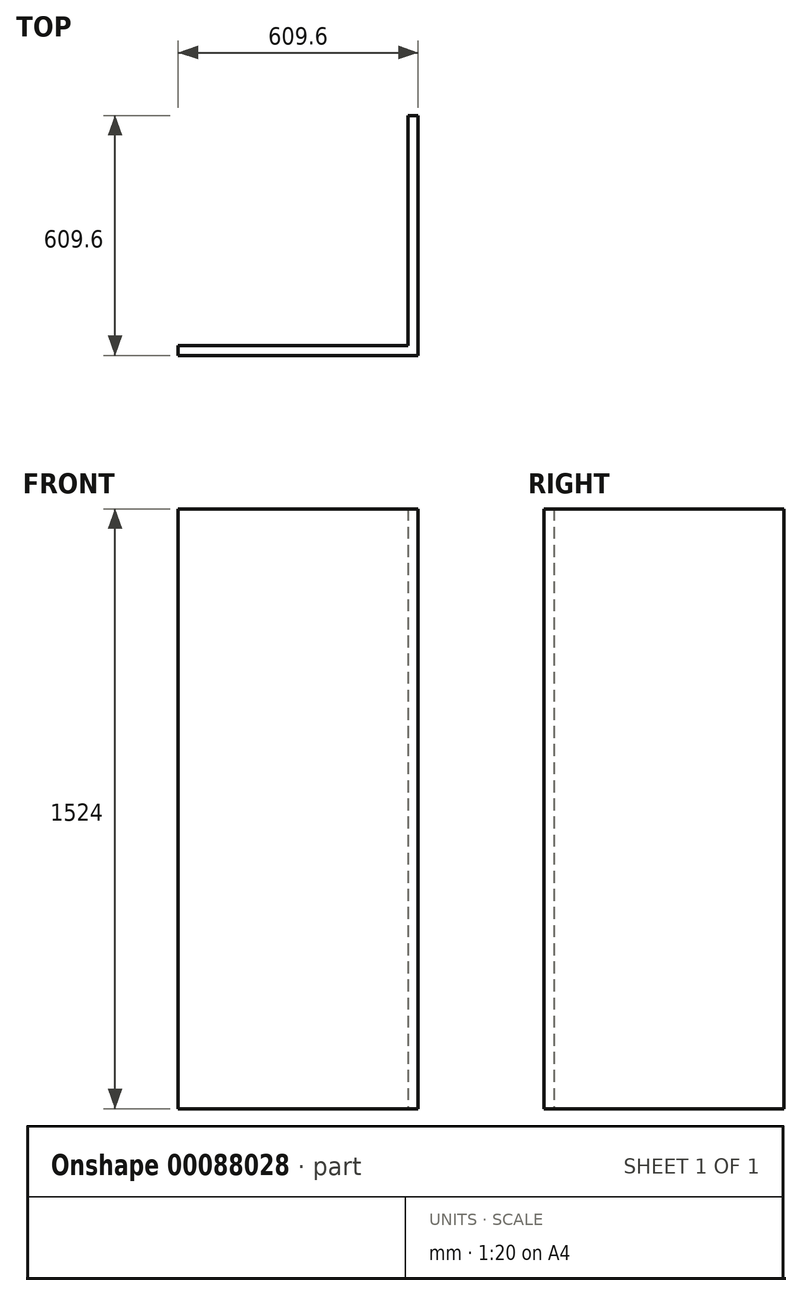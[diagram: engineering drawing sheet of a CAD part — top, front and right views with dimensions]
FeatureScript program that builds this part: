
annotation { "Feature Type Name" : "Feature", "Feature Type Description" : "" }
export const myFeature = defineFeature(function(context is Context, id is Id, definition is map)
    precondition{}
    {
        {
            var Q0;
            Q0=qCreatedBy(makeId("Top.planeOp"),FACE);
            var sketch = newSketch(context, id + "F0", { "sketchPlane" : qUnion([Q0])});
            skLineSegment(sketch, "E0", {"start": v(0, 0) * mm, "end": v(-609.6, 0) * mm});
            skLineSegment(sketch, "E1", {"start": v(0, 609.6) * mm, "end": v(0, 0) * mm});
            skLineSegment(sketch, "E2", {"start": v(-25.4, 609.6) * mm, "end": v(-25.4, 25.4) * mm});
            skLineSegment(sketch, "E3", {"start": v(-25.4, 25.4) * mm, "end": v(-609.6, 25.4) * mm});
            skLineSegment(sketch, "E4", {"start": v(-609.6, 0) * mm, "end": v(-609.6, 25.4) * mm});
            skLineSegment(sketch, "E5", {"start": v(-25.4, 609.6) * mm, "end": v(0, 609.6) * mm});
            skLineSegment(sketch, "E6", {"start": v(-180.41, 25.4) * mm, "end": v(-180.41, 0) * mm, "construction": true});
            skLineSegment(sketch, "E7", {"start": v(-25.4, 131.67) * mm, "end": v(0, 131.67) * mm, "construction": true});
            skSolve(sketch);
        }
        {
            var Q0;
            Q0=makeQuery(id+"F0.imprint","IMPRINT",FACE,{"disambiguationData":[TD([[makeQuery(id+"F0.imprint","IMPRINT",EDGE,{"derivedFrom":sQuery(id+"F0.wireOp",EDGE,"E0")}),-1.0]])]});
            extrude(context, id + "F1", {"entities" : qUnion([Q0]), "depth" : 1524 * mm});
        }
    });
